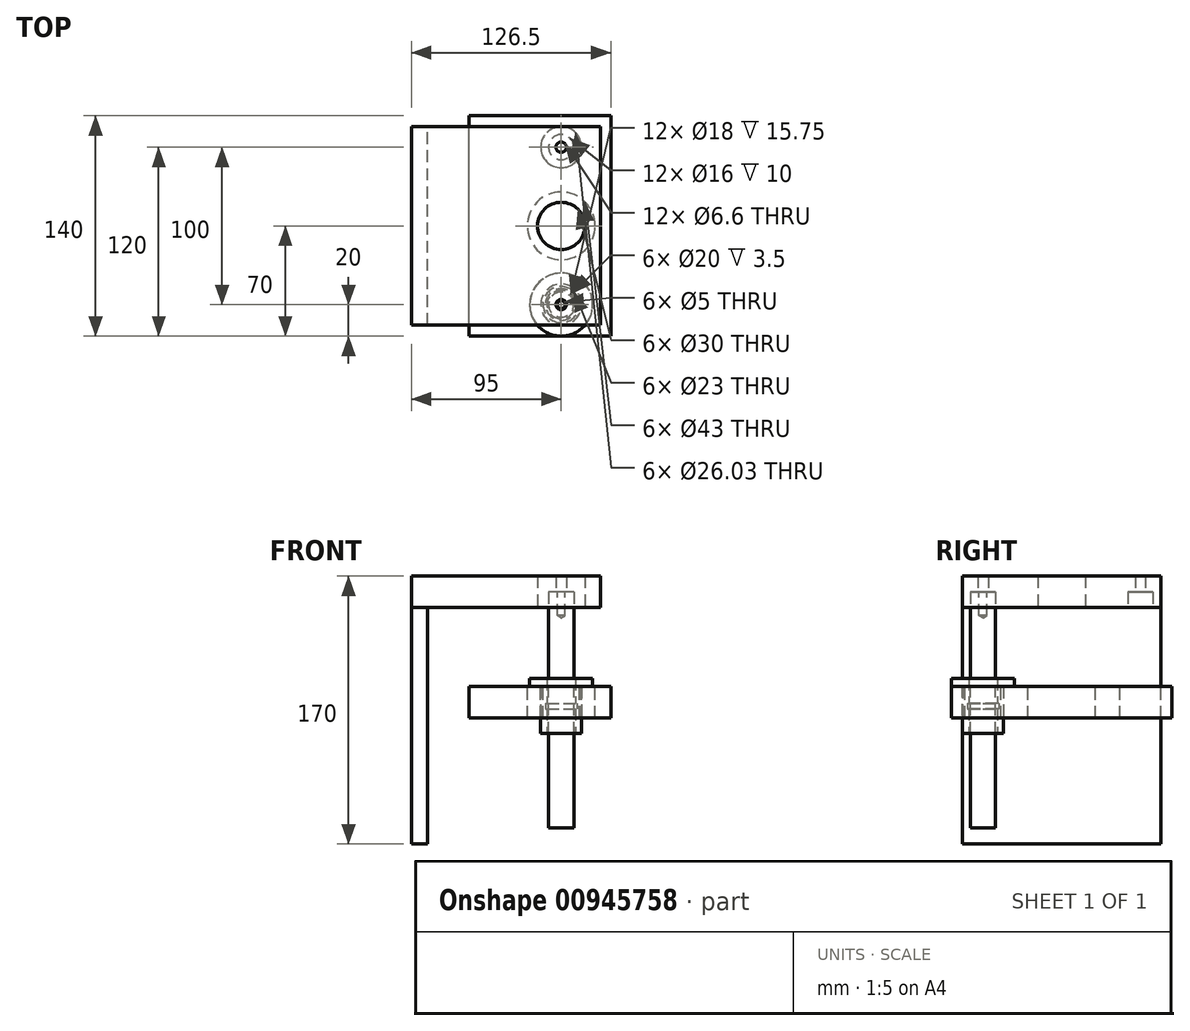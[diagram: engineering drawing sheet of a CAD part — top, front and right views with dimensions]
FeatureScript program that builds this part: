
annotation { "Feature Type Name" : "Feature", "Feature Type Description" : "" }
export const myFeature = defineFeature(function(context is Context, id is Id, definition is map)
    precondition{}
    {
        {
            var Q0;
            Q0=qCreatedBy(makeId("Top.planeOp"),FACE);
            var sketch = newSketch(context, id + "F0", { "sketchPlane" : qUnion([Q0])});
            skLineSegment(sketch, "E0.bottom", {"start": v(-95, 63) * mm, "end": v(25, 63) * mm});
            skLineSegment(sketch, "E0.top", {"start": v(-95, -63) * mm, "end": v(25, -63) * mm});
            skLineSegment(sketch, "E0.left", {"start": v(-95, 63) * mm, "end": v(-95, -63) * mm});
            skLineSegment(sketch, "E0.right", {"start": v(25, 63) * mm, "end": v(25, -63) * mm});
            skCircle(sketch, "E1", {"center": v(0, 0) * mm, "radius": 15 * mm});
            skCircle(sketch, "E2", {"center": v(0, 50) * mm, "radius": 8 * mm});
            skCircle(sketch, "E3", {"center": v(0, -50) * mm, "radius": 8 * mm});
            skSolve(sketch);
        }
        {
            var Q0;
            Q0=makeQuery(id+"F0.imprint","IMPRINT",FACE,{"disambiguationData":[TD([[makeQuery(id+"F0.imprint","IMPRINT",EDGE,{"derivedFrom":sQuery(id+"F0.wireOp",EDGE,"E0.bottom")}),-1.0]])]});
            var Q1;
            Q1=makeQuery(id+"F0.imprint","IMPRINT",FACE,{"disambiguationData":[TD([[makeQuery(id+"F0.imprint","IMPRINT",EDGE,{"derivedFrom":sQuery(id+"F0.wireOp",EDGE,"E3")}),1.0]])]});
            var Q2;
            Q2=makeQuery(id+"F0.imprint","IMPRINT",FACE,{"disambiguationData":[TD([[makeQuery(id+"F0.imprint","IMPRINT",EDGE,{"derivedFrom":sQuery(id+"F0.wireOp",EDGE,"E2")}),1.0]])]});
            extrude(context, id + "F1", {"entities" : qUnion([Q0, Q1, Q2]), "depth" : 20 * mm, "offsetDistance" : 25 * mm});
        }
        {
            var Q0;
            Q0=makeQuery(id+"F0.imprint","IMPRINT",FACE,{"disambiguationData":[TD([[makeQuery(id+"F0.imprint","IMPRINT",EDGE,{"derivedFrom":sQuery(id+"F0.wireOp",EDGE,"E3")}),1.0]])]});
            var Q1;
            Q1=makeQuery(id+"F0.imprint","IMPRINT",FACE,{"disambiguationData":[TD([[makeQuery(id+"F0.imprint","IMPRINT",EDGE,{"derivedFrom":sQuery(id+"F0.wireOp",EDGE,"E2")}),1.0]])]});
            extrude(context, id + "F2", {"entities" : qUnion([Q0, Q1]), "operationType" : NewBodyOperationType.REMOVE, "depth" : 10 * mm, "offsetDistance" : 25 * mm});
        }
        {
            var Q0;
            Q0=sQuery(id+"F0.wireOp",VERTEX,"E3.center");
            var Q1;
            Q1=sQuery(id+"F0.wireOp",VERTEX,"E2.center");
            var Q2;
            Q2=makeQuery(id+"F1.opExtrude","SWEPT_BODY",BODY,{"disambiguationData":[OSD([sQuery(id+"F0.wireOp",EDGE,"E0.bottom"),sQuery(id+"F0.wireOp",EDGE,"E0.top"),sQuery(id+"F0.wireOp",EDGE,"E0.left"),sQuery(id+"F0.wireOp",EDGE,"E0.right"),sQuery(id+"F0.wireOp",EDGE,"E1")])]});
            hole(context, id + "F3", {"style" : HoleStyle.SIMPLE, "endStyle" : HoleEndStyle.THROUGH, "oppositeDirection" : true, "standardTappedOrClearance" : lookupTablePath({ "fit" : "Normal", "standard" : "ISO", "size" : "M6", "type" : "Clearance" }), "standardBlindInLast" : lookupTablePath({ "fit" : "Normal", "standard" : "ISO", "engagement" : "75%", "pitch" : "1 mm", "size" : "M6", "type" : "Clearance & tapped" }), "holeDiameter" : 6.6 * mm, "majorDiameter" : 6 * mm, "isTappedThrough" : true, "tappedDepth" : 10.6 * mm, "tapClearance" : 3, "locations" : qUnion([Q0, Q1]), "scope" : qUnion([Q2])});
        }
        {
            var Q0;
            Q0=makeQuery(id+"F2.boolean.opBoolean","COPY",FACE,{"derivedFrom":makeQuery(id+"F2.opExtrude","CAP_FACE",FACE,{"disambiguationData":[OSD([sQuery(id+"F0.wireOp",EDGE,"E3")])],"isStart":false})});
            var sketch = newSketch(context, id + "F4", { "sketchPlane" : qUnion([Q0])});
            skCircle(sketch, "E4.0", {"center": v(0, 50) * mm, "radius": 8 * mm});
            skSolve(sketch);
        }
        {
            var Q0;
            Q0 = qSketchRegion(id + "F4", true);
            extrude(context, id + "F5", {"entities" : qUnion([Q0]), "depth" : 150 * mm, "offsetDistance" : 25 * mm});
        }
        {
            var Q0;
            Q0=makeQuery(id+"F5.opExtrude","CAP_FACE",FACE,{"disambiguationData":[OSD([sQuery(id+"F4.wireOp",EDGE,"E4.0")])],"isStart":true});
            var sketch = newSketch(context, id + "F6", { "sketchPlane" : qUnion([Q0])});
            skCircle(sketch, "E5.0", {"center": v(0, -50) * mm, "radius": 8 * mm});
            skSolve(sketch);
        }
        {
            var Q0;
            Q0=sQuery(id+"F6.wireOp",VERTEX,"E5.0.center");
            var Q1;
            Q1=makeQuery(id+"F5.opExtrude","SWEPT_BODY",BODY,{"disambiguationData":[OSD([sQuery(id+"F4.wireOp",EDGE,"E4.0")])]});
            hole(context, id + "F7", {"style" : HoleStyle.SIMPLE, "endStyle" : HoleEndStyle.BLIND, "standardTappedOrClearance" : lookupTablePath({ "standard" : "ISO", "engagement" : "75%", "pitch" : "1 mm", "size" : "M6", "type" : "Tapped" }), "standardBlindInLast" : lookupTablePath({ "standard" : "ISO", "fit" : "Normal", "engagement" : "75%", "pitch" : "1 mm", "size" : "M6", "type" : "Clearance & tapped" }), "holeDiameter" : 5 * mm, "majorDiameter" : 6 * mm, "showTappedDepth" : true, "holeDepth" : 15 * mm, "isTappedThrough" : true, "tappedDepth" : 12 * mm, "tapClearance" : 3, "locations" : qUnion([Q0]), "scope" : qUnion([Q1])});
        }
        {
            var Q0;
            Q0=makeQuery(id+"F1.opExtrude","CAP_FACE",FACE,{"disambiguationData":[OSD([sQuery(id+"F0.wireOp",EDGE,"E0.bottom"),sQuery(id+"F0.wireOp",EDGE,"E0.top"),sQuery(id+"F0.wireOp",EDGE,"E0.left"),sQuery(id+"F0.wireOp",EDGE,"E0.right"),sQuery(id+"F0.wireOp",EDGE,"E1")])],"isStart":true});
            var sketch = newSketch(context, id + "F8", { "sketchPlane" : qUnion([Q0])});
            skLineSegment(sketch, "E6.0.0", {"start": v(-95, 63) * mm, "end": v(-95, -63) * mm});
            skLineSegment(sketch, "E6.0.1", {"start": v(-95, -63) * mm, "end": v(25, -63) * mm});
            skLineSegment(sketch, "E6.0.2", {"start": v(25, -63) * mm, "end": v(25, 63) * mm});
            skLineSegment(sketch, "E6.0.3", {"start": v(25, 63) * mm, "end": v(-95, 63) * mm});
            skLineSegment(sketch, "E7", {"start": v(-85, 63) * mm, "end": v(-85, -63) * mm});
            skSolve(sketch);
        }
        {
            var Q0;
            {var subQ0=sQuery(id+"F8.wireOp",EDGE,"E6.0.0");Q0=makeQuery(id+"F8.imprint","IMPRINT",FACE,{"disambiguationData":[TD([[makeQuery(id+"F8.imprint","IMPRINT",EDGE,{"derivedFrom":subQ0}),-1.0]])]});}
            extrude(context, id + "F9", {"entities" : qUnion([Q0]), "depth" : 150 * mm, "offsetDistance" : 25 * mm});
        }
        {
            var Q0;
            Q0=makeQuery(id+"F1.opExtrude","CAP_FACE",FACE,{"disambiguationData":[OSD([sQuery(id+"F0.wireOp",EDGE,"E0.bottom"),sQuery(id+"F0.wireOp",EDGE,"E0.top"),sQuery(id+"F0.wireOp",EDGE,"E0.left"),sQuery(id+"F0.wireOp",EDGE,"E0.right"),sQuery(id+"F0.wireOp",EDGE,"E1")])],"isStart":true});
            cPlane(context, id + "F10", {"entities" : qUnion([Q0]), "cplaneType" : CPlaneType.OFFSET, "offset" : 50 * mm, "width" : 150 * mm, "height" : 150 * mm});
        }
        {
            var Q0;
            Q0=qCreatedBy(id+"F10.planeOp",FACE);
            var sketch = newSketch(context, id + "F11", { "sketchPlane" : qUnion([Q0])});
            skCircle(sketch, "E8.0", {"center": v(0, 50) * mm, "radius": 8 * mm});
            skCircle(sketch, "E9.0", {"center": v(0, -50) * mm, "radius": 8 * mm});
            skCircle(sketch, "E10.0", {"center": v(0, 0) * mm, "radius": 15 * mm});
            skCircle(sketch, "E11", {"center": v(0, 50) * mm, "radius": 11.5 * mm});
            skCircle(sketch, "E12", {"center": v(0, 0) * mm, "radius": 21.5 * mm});
            skCircle(sketch, "E13", {"center": v(0, -50) * mm, "radius": 13.01 * mm});
            skLineSegment(sketch, "E14.bottom", {"start": v(-58.5, 70) * mm, "end": v(31.5, 70) * mm});
            skLineSegment(sketch, "E14.top", {"start": v(-58.5, -70) * mm, "end": v(31.5, -70) * mm});
            skLineSegment(sketch, "E14.left", {"start": v(-58.5, 70) * mm, "end": v(-58.5, -70) * mm});
            skLineSegment(sketch, "E14.right", {"start": v(31.5, 70) * mm, "end": v(31.5, -70) * mm});
            skSolve(sketch);
        }
        {
            var Q0;
            Q0=makeQuery(id+"F11.imprint","IMPRINT",FACE,{"disambiguationData":[TD([[makeQuery(id+"F11.imprint","IMPRINT",EDGE,{"derivedFrom":sQuery(id+"F11.wireOp",EDGE,"E11")}),-1.0]])]});
            extrude(context, id + "F12", {"entities" : qUnion([Q0]), "depth" : 20 * mm, "offsetDistance" : 25 * mm});
        }
        {
            var Q0;
            Q0=qCreatedBy(makeId("Right.planeOp"),FACE);
            var sketch = newSketch(context, id + "F13", { "sketchPlane" : qUnion([Q0])});
            skLineSegment(sketch, "E15", {"start": v(-58, -140) * mm, "end": v(-58, 10) * mm, "construction": true});
            skLineSegment(sketch, "E16", {"start": v(-42, 10) * mm, "end": v(-42, -140) * mm, "construction": true});
            skLineSegment(sketch, "E17.0", {"start": v(-70, -50) * mm, "end": v(70, -50) * mm, "construction": true});
            skLineSegment(sketch, "E18.0", {"start": v(-70, -70) * mm, "end": v(70, -70) * mm, "construction": true});
            skLineSegment(sketch, "E19", {"start": v(-63, -80) * mm, "end": v(-63, -50) * mm});
            skLineSegment(sketch, "E20", {"start": v(-63, -50) * mm, "end": v(-70, -50) * mm});
            skLineSegment(sketch, "E21", {"start": v(-70, -50) * mm, "end": v(-70, -45) * mm});
            skLineSegment(sketch, "E22", {"start": v(-70, -45) * mm, "end": v(-59, -45) * mm});
            skLineSegment(sketch, "E23", {"start": v(-59, -45) * mm, "end": v(-59, -60.75) * mm});
            skLineSegment(sketch, "E24", {"start": v(-59, -80) * mm, "end": v(-63, -80) * mm});
            skLineSegment(sketch, "E25", {"start": v(-58, 0) * mm, "end": v(-58, 10) * mm, "construction": true});
            skLineSegment(sketch, "E26", {"start": v(-42, 10) * mm, "end": v(-42, 0) * mm, "construction": true});
            skLineSegment(sketch, "E27.0", {"start": v(-58, -140) * mm, "end": v(-42, -140) * mm, "construction": true});
            skLineSegment(sketch, "E28", {"start": v(-50, -140) * mm, "end": v(-50, -30.94) * mm, "construction": true});
            skLineSegment(sketch, "E29", {"start": v(-59, -60.75) * mm, "end": v(-60, -60.75) * mm});
            skLineSegment(sketch, "E30", {"start": v(-60, -60.75) * mm, "end": v(-60, -64.25) * mm});
            skLineSegment(sketch, "E31", {"start": v(-60, -64.25) * mm, "end": v(-59, -64.25) * mm});
            skLineSegment(sketch, "E32.trimOffspring", {"start": v(-59, -64.25) * mm, "end": v(-59, -80) * mm});
            skLineSegment(sketch, "E33", {"start": v(-60, -62.5) * mm, "end": v(-56.94, -62.5) * mm, "construction": true});
            skSolve(sketch);
        }
        {
            var Q0;
            Q0=makeQuery(id+"F13.imprint","IMPRINT",FACE,{"disambiguationData":[TD([[makeQuery(id+"F13.imprint","IMPRINT",EDGE,{"derivedFrom":sQuery(id+"F13.wireOp",EDGE,"E19")}),-1.0]])]});
            var Q1;
            Q1=sQuery(id+"F13.wireOp",EDGE,"E28");
            revolve(context, id + "F14", {"surfaceOperationType" : NewSurfaceOperationType.NEW, "entities" : qUnion([Q0]), "axis" : qUnion([Q1]), "revolveType" : RevolveType.FULL});
        }
    });
